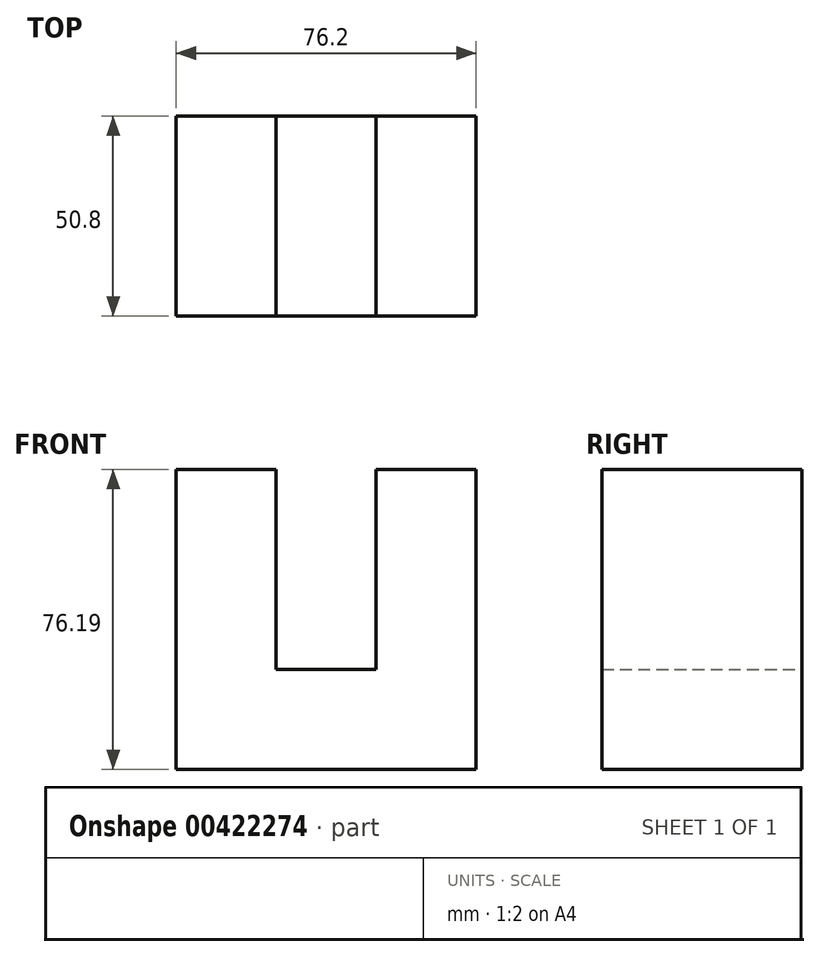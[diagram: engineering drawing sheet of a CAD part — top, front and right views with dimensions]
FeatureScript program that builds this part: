
annotation { "Feature Type Name" : "Feature", "Feature Type Description" : "" }
export const myFeature = defineFeature(function(context is Context, id is Id, definition is map)
    precondition{}
    {
        {
            var Q0;
            Q0=qCreatedBy(makeId("Front.planeOp"),FACE);
            var sketch = newSketch(context, id + "F0", { "sketchPlane" : qUnion([Q0])});
            skLineSegment(sketch, "E0", {"start": v(47.17, 35.33) * mm, "end": v(47.17, -40.86) * mm});
            skLineSegment(sketch, "E1", {"start": v(47.17, -40.86) * mm, "end": v(-29.03, -40.86) * mm});
            skLineSegment(sketch, "E2", {"start": v(-29.03, -40.86) * mm, "end": v(-29.03, 35.33) * mm});
            skLineSegment(sketch, "E3", {"start": v(-29.03, 35.33) * mm, "end": v(-3.63, 35.33) * mm});
            skLineSegment(sketch, "E4", {"start": v(-3.63, 35.33) * mm, "end": v(-3.63, -15.47) * mm});
            skLineSegment(sketch, "E5", {"start": v(-3.63, -15.47) * mm, "end": v(21.77, -15.47) * mm});
            skLineSegment(sketch, "E6", {"start": v(21.77, -15.47) * mm, "end": v(21.77, 35.33) * mm});
            skLineSegment(sketch, "E7", {"start": v(21.77, 35.33) * mm, "end": v(47.17, 35.33) * mm});
            skSolve(sketch);
        }
        {
            var Q0;
            Q0=makeQuery(id+"F0.imprint","IMPRINT",FACE,{"disambiguationData":[TD([[makeQuery(id+"F0.imprint","IMPRINT",EDGE,{"derivedFrom":sQuery(id+"F0.wireOp",EDGE,"E0")}),-1.0]])]});
            extrude(context, id + "F1", {"entities" : qUnion([Q0]), "depth" : 50.8 * mm});
        }
    });
